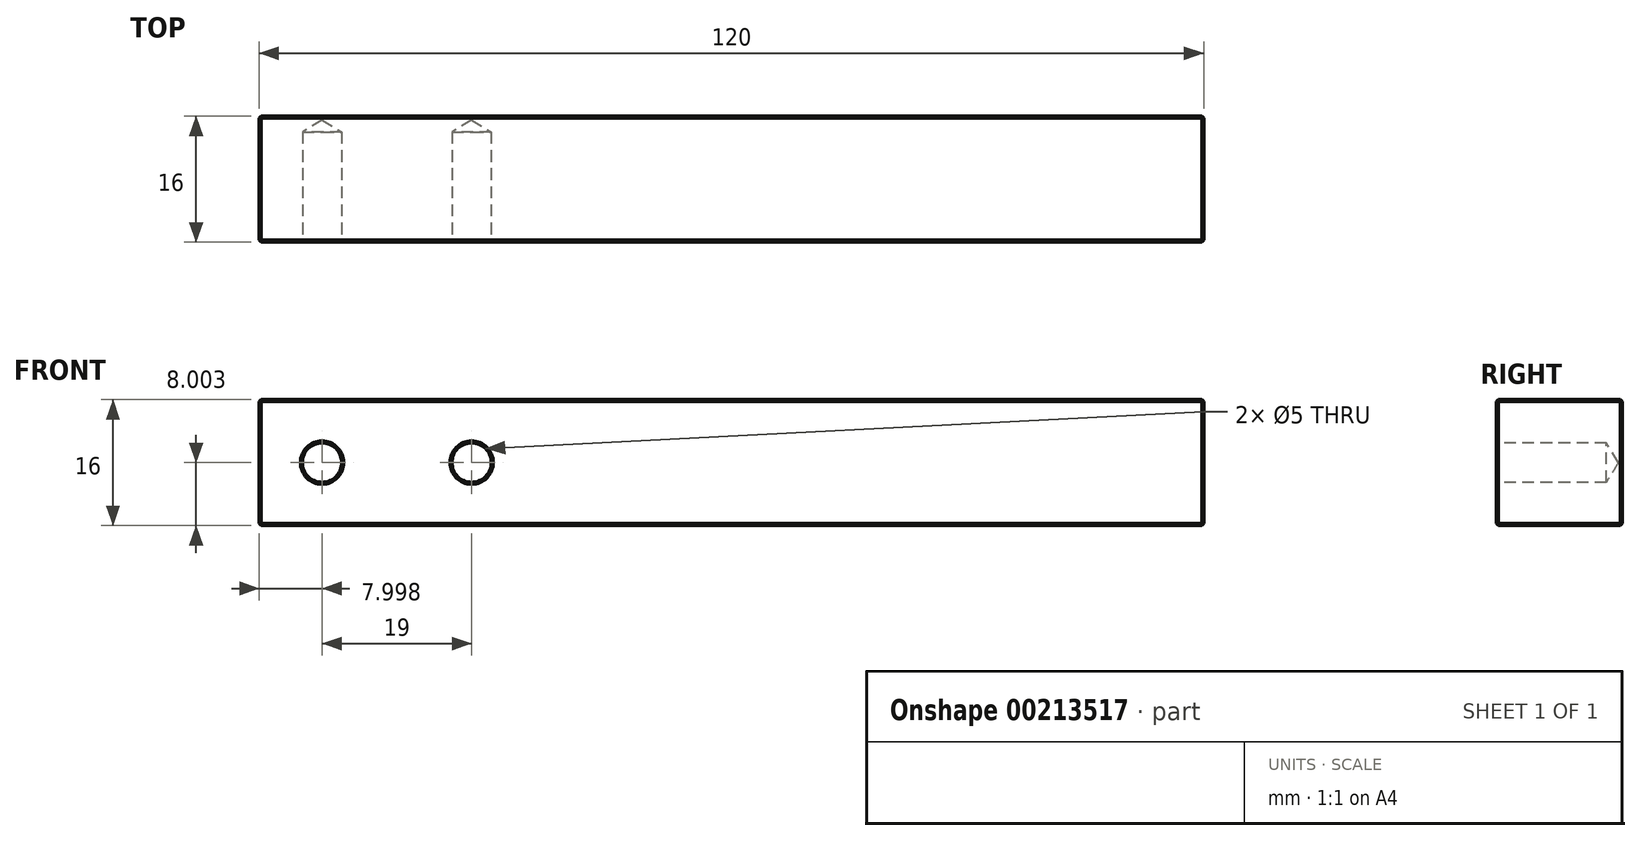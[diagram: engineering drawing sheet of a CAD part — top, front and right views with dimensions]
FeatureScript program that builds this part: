
annotation { "Feature Type Name" : "Feature", "Feature Type Description" : "" }
export const myFeature = defineFeature(function(context is Context, id is Id, definition is map)
    precondition{}
    {
        {
            var Q0;
            Q0=qCreatedBy(makeId("Front.planeOp"),FACE);
            var sketch = newSketch(context, id + "F0", { "sketchPlane" : qUnion([Q0])});
            skLineSegment(sketch, "E0.bottom", {"start": v(-44.26, 4.7) * mm, "end": v(75.74, 4.7) * mm});
            skLineSegment(sketch, "E0.top", {"start": v(-44.26, -11.3) * mm, "end": v(75.74, -11.3) * mm});
            skLineSegment(sketch, "E0.left", {"start": v(-44.26, 4.7) * mm, "end": v(-44.26, -11.3) * mm});
            skLineSegment(sketch, "E0.right", {"start": v(75.74, 4.7) * mm, "end": v(75.74, -11.3) * mm});
            skSolve(sketch);
        }
        {
            var Q0;
            Q0 = qSketchRegion(id + "F0", true);
            extrude(context, id + "F1", {"entities" : qUnion([Q0]), "depth" : 16 * mm});
        }
        {
            var Q0;
            Q0=makeQuery(id+"F1.opExtrude","CAP_FACE",FACE,{"disambiguationData":[OSD([sQuery(id+"F0.wireOp",EDGE,"E0.bottom"),sQuery(id+"F0.wireOp",EDGE,"E0.top"),sQuery(id+"F0.wireOp",EDGE,"E0.left"),sQuery(id+"F0.wireOp",EDGE,"E0.right")])],"isStart":false});
            var sketch = newSketch(context, id + "F2", { "sketchPlane" : qUnion([Q0])});
            skPoint(sketch, "E1", {"position": v(-36.26, -3.3) * mm});
            skPoint(sketch, "E1.positionSnap0", {"position": v(-44.26, -3.3) * mm});
            skPoint(sketch, "E2", {"position": v(-17.26, -3.3) * mm});
            skSolve(sketch);
        }
        {
            var Q0;
            Q0=sQuery(id+"F2.wireOp",VERTEX,"E2");
            var Q1;
            Q1=sQuery(id+"F2.wireOp",VERTEX,"E1");
            var Q2;
            Q2=makeQuery(id+"F1.opExtrude","SWEPT_BODY",BODY,{"disambiguationData":[OSD([sQuery(id+"F0.wireOp",EDGE,"E0.bottom"),sQuery(id+"F0.wireOp",EDGE,"E0.top"),sQuery(id+"F0.wireOp",EDGE,"E0.left"),sQuery(id+"F0.wireOp",EDGE,"E0.right")])]});
            hole(context, id + "F3", {"style" : HoleStyle.SIMPLE, "endStyle" : HoleEndStyle.BLIND, "standardTappedOrClearance" : lookupTablePath({ "standard" : "ISO", "engagement" : "75%", "pitch" : "1 mm", "size" : "M6", "type" : "Tapped" }), "standardBlindInLast" : lookupTablePath({ "standard" : "ISO", "engagement" : "75%", "pitch" : "1 mm", "size" : "M6", "type" : "Tapped" }), "holeDiameter" : 5 * mm, "holeDepth" : 14 * mm, "locations" : qUnion([Q0, Q1]), "scope" : qUnion([Q2]), "majorDiameter" : 6 * mm});
        }
        {
            var Q0;
            Q0=makeQuery(id+"F1.opExtrude","SWEPT_FACE",FACE,{"disambiguationData":[OSD([sQuery(id+"F0.wireOp",EDGE,"E0.bottom")])]});
            var Q1;
            Q1=makeQuery(id+"F1.opExtrude","CAP_FACE",FACE,{"disambiguationData":[OSD([sQuery(id+"F0.wireOp",EDGE,"E0.bottom"),sQuery(id+"F0.wireOp",EDGE,"E0.top"),sQuery(id+"F0.wireOp",EDGE,"E0.left"),sQuery(id+"F0.wireOp",EDGE,"E0.right")])],"isStart":false});
            var Q2;
            Q2=makeQuery(id+"F1.opExtrude","SWEPT_FACE",FACE,{"disambiguationData":[OSD([sQuery(id+"F0.wireOp",EDGE,"E0.left")])]});
            var Q3;
            Q3=makeQuery(id+"F1.opExtrude","CAP_FACE",FACE,{"disambiguationData":[OSD([sQuery(id+"F0.wireOp",EDGE,"E0.bottom"),sQuery(id+"F0.wireOp",EDGE,"E0.top"),sQuery(id+"F0.wireOp",EDGE,"E0.left"),sQuery(id+"F0.wireOp",EDGE,"E0.right")])],"isStart":true});
            var Q4;
            Q4=makeQuery(id+"F1.opExtrude","SWEPT_FACE",FACE,{"disambiguationData":[OSD([sQuery(id+"F0.wireOp",EDGE,"E0.right")])]});
            var Q5;
            Q5=makeQuery(id+"F1.opExtrude","SWEPT_FACE",FACE,{"disambiguationData":[OSD([sQuery(id+"F0.wireOp",EDGE,"E0.top")])]});
            chamfer(context, id + "F4", {"entities" : qUnion([Q0, Q1, Q2, Q3, Q4, Q5]), "width" : 0.25 * mm, "tangentPropagation" : true});
        }
    });
